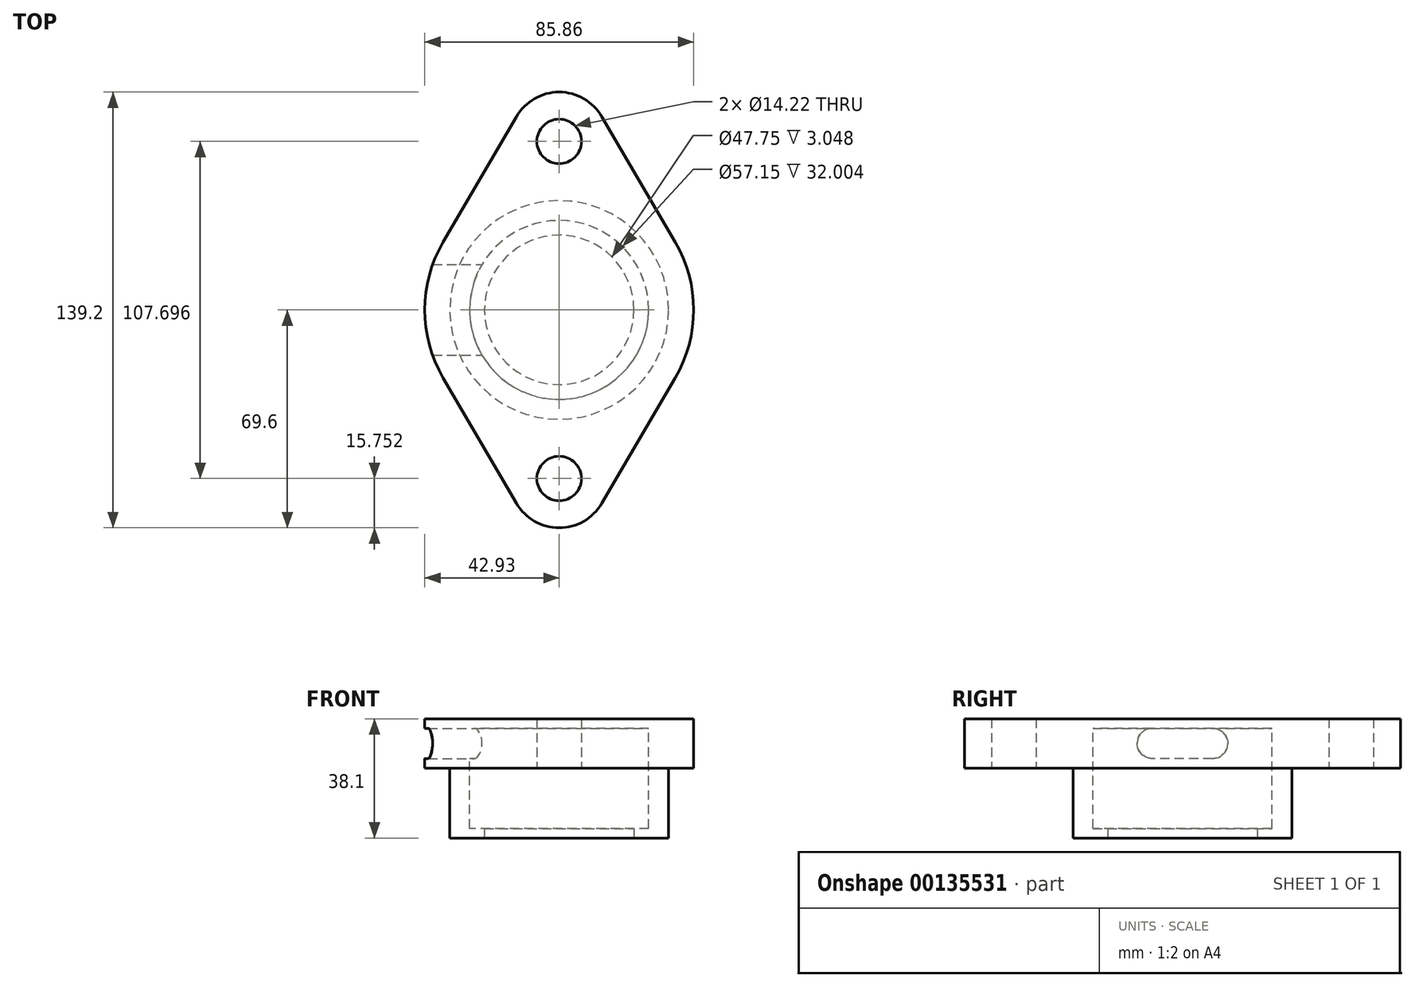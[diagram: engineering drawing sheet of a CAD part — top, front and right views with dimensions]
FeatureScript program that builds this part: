
annotation { "Feature Type Name" : "Feature", "Feature Type Description" : "" }
export const myFeature = defineFeature(function(context is Context, id is Id, definition is map)
    precondition{}
    {
        {
            var Q0;
            Q0=qCreatedBy(makeId("Top.planeOp"),FACE);
            var sketch = newSketch(context, id + "F0", { "sketchPlane" : qUnion([Q0])});
            skCircle(sketch, "E0", {"center": v(0, 0) * mm, "radius": 28.58 * mm});
            skCircle(sketch, "E1", {"center": v(0, 0) * mm, "radius": 34.93 * mm});
            skSolve(sketch);
        }
        {
            var Q0;
            Q0=makeQuery(id+"F0.imprint","IMPRINT",FACE,{"disambiguationData":[TD([[makeQuery(id+"F0.imprint","IMPRINT",EDGE,{"derivedFrom":sQuery(id+"F0.wireOp",EDGE,"E0")}),1.0]])]});
            var Q1;
            Q1=makeQuery(id+"F0.imprint","IMPRINT",FACE,{"disambiguationData":[TD([[makeQuery(id+"F0.imprint","IMPRINT",EDGE,{"derivedFrom":sQuery(id+"F0.wireOp",EDGE,"E0")}),-1.0]])]});
            extrude(context, id + "F1", {"entities" : qUnion([Q0, Q1]), "oppositeDirection" : true, "depth" : 22.35 * mm});
        }
        {
            var Q0;
            Q0=makeQuery(id+"F1.opExtrude","CAP_FACE",FACE,{"disambiguationData":[OSD([sQuery(id+"F0.wireOp",EDGE,"E0"),sQuery(id+"F0.wireOp",EDGE,"E1")])],"isStart":true});
            var sketch = newSketch(context, id + "F2", { "sketchPlane" : qUnion([Q0])});
            skCircle(sketch, "E2", {"center": v(0, 53.85) * mm, "radius": 7.11 * mm});
            skCircle(sketch, "E3", {"center": v(0, -53.85) * mm, "radius": 7.11 * mm});
            skArc(sketch, "E4", {"start": v(-13.6, -61.8) * mm, "mid": v(0, -69.6) * mm, "end": v(13.6, -61.8) * mm});
            skArc(sketch, "E5", {"start": v(13.6, 61.8) * mm, "mid": v(0, 69.6) * mm, "end": v(-13.6, 61.8) * mm});
            skLineSegment(sketch, "E6", {"start": v(-13.6, 61.8) * mm, "end": v(-37.06, 21.67) * mm});
            skLineSegment(sketch, "E7", {"start": v(13.6, 61.8) * mm, "end": v(37.06, 21.67) * mm});
            skLineSegment(sketch, "E8", {"start": v(-13.6, -61.8) * mm, "end": v(-37.06, -21.67) * mm});
            skLineSegment(sketch, "E9", {"start": v(13.6, -61.8) * mm, "end": v(37.06, -21.67) * mm});
            skArc(sketch, "E10", {"start": v(-37.06, 21.67) * mm, "mid": v(-42.93, 0) * mm, "end": v(-37.06, -21.67) * mm});
            skArc(sketch, "E11", {"start": v(37.06, -21.67) * mm, "mid": v(42.93, 0) * mm, "end": v(37.06, 21.67) * mm});
            skSolve(sketch);
        }
        {
            var Q0;
            Q0=makeQuery(id+"F2.imprint","IMPRINT",FACE,{"disambiguationData":[TD([[makeQuery(id+"F2.imprint","IMPRINT",EDGE,{"derivedFrom":sQuery(id+"F2.wireOp",EDGE,"E2")}),-1.0]])]});
            extrude(context, id + "F3", {"entities" : qUnion([Q0]), "depth" : 15.75 * mm});
        }
        {
            var Q0;
            Q0=makeQuery(id+"F1.opExtrude","CAP_FACE",FACE,{"disambiguationData":[OSD([sQuery(id+"F0.wireOp",EDGE,"E0"),sQuery(id+"F0.wireOp",EDGE,"E1")])],"isStart":false});
            cPlane(context, id + "F4", {"entities" : qUnion([Q0]), "cplaneType" : CPlaneType.OFFSET, "offset" : 0 * mm, "width" : 152.4 * mm, "height" : 152.4 * mm});
        }
        {
            var Q0;
            Q0=qCreatedBy(id+"F4.planeOp",FACE);
            var sketch = newSketch(context, id + "F5", { "sketchPlane" : qUnion([Q0])});
            skCircle(sketch, "E12", {"center": v(0, 0) * mm, "radius": 23.88 * mm});
            skSolve(sketch);
        }
        {
            var Q0;
            Q0=makeQuery(id+"F5.imprint","IMPRINT",FACE,{"disambiguationData":[TD([[makeQuery(id+"F5.imprint","IMPRINT",EDGE,{"derivedFrom":sQuery(id+"F5.wireOp",EDGE,"E12")}),1.0]])]});
            extrude(context, id + "F6", {"entities" : qUnion([Q0]), "operationType" : NewBodyOperationType.REMOVE, "oppositeDirection" : true, "depth" : 3.05 * mm});
        }
        {
            var Q0;
            Q0=makeQuery(id+"F0.imprint","IMPRINT",FACE,{"disambiguationData":[TD([[makeQuery(id+"F0.imprint","IMPRINT",EDGE,{"derivedFrom":sQuery(id+"F0.wireOp",EDGE,"E0")}),1.0]])]});
            extrude(context, id + "F7", {"entities" : qUnion([Q0]), "operationType" : NewBodyOperationType.REMOVE, "oppositeDirection" : true, "depth" : 19.3 * mm});
        }
        {
            var Q0;
            Q0=makeQuery(id+"F0.imprint","IMPRINT",FACE,{"disambiguationData":[TD([[makeQuery(id+"F0.imprint","IMPRINT",EDGE,{"derivedFrom":sQuery(id+"F0.wireOp",EDGE,"E0")}),1.0]])]});
            var Q1;
            Q1=makeQuery(id+"F0.imprint","IMPRINT",FACE,{"disambiguationData":[TD([[makeQuery(id+"F0.imprint","IMPRINT",EDGE,{"derivedFrom":sQuery(id+"F0.wireOp",EDGE,"E0")}),-1.0]])]});
            extrude(context, id + "F8", {"entities" : qUnion([Q0, Q1]), "operationType" : NewBodyOperationType.ADD, "depth" : 15.75 * mm});
        }
        {
            var Q0;
            Q0=makeQuery(id+"F0.imprint","IMPRINT",FACE,{"disambiguationData":[TD([[makeQuery(id+"F0.imprint","IMPRINT",EDGE,{"derivedFrom":sQuery(id+"F0.wireOp",EDGE,"E0")}),1.0]])]});
            extrude(context, id + "F9", {"entities" : qUnion([Q0]), "operationType" : NewBodyOperationType.REMOVE, "depth" : 12.7 * mm});
        }
        {
            var Q0;
            Q0=qCreatedBy(makeId("Right.planeOp"),FACE);
            var sketch = newSketch(context, id + "F10", { "sketchPlane" : qUnion([Q0])});
            skLineSegment(sketch, "E13", {"start": v(0, -45.35) * mm, "end": v(0, 29.94) * mm, "construction": true});
            skLineSegment(sketch, "E14", {"start": v(9.65, 12.7) * mm, "end": v(-9.65, 12.7) * mm});
            skLineSegment(sketch, "E15", {"start": v(9.65, 3.05) * mm, "end": v(-9.65, 3.05) * mm});
            skArc(sketch, "E16", {"start": v(-9.65, 12.7) * mm, "mid": v(-14.48, 7.87) * mm, "end": v(-9.65, 3.05) * mm});
            skArc(sketch, "E17", {"start": v(9.65, 12.7) * mm, "mid": v(14.48, 7.87) * mm, "end": v(9.65, 3.05) * mm});
            skSolve(sketch);
        }
        {
            var Q0;
            Q0 = qSketchRegion(id + "F10", true);
            extrude(context, id + "F11", {"entities" : qUnion([Q0]), "operationType" : NewBodyOperationType.REMOVE, "oppositeDirection" : true, "depth" : 54.1 * mm});
        }
    });
